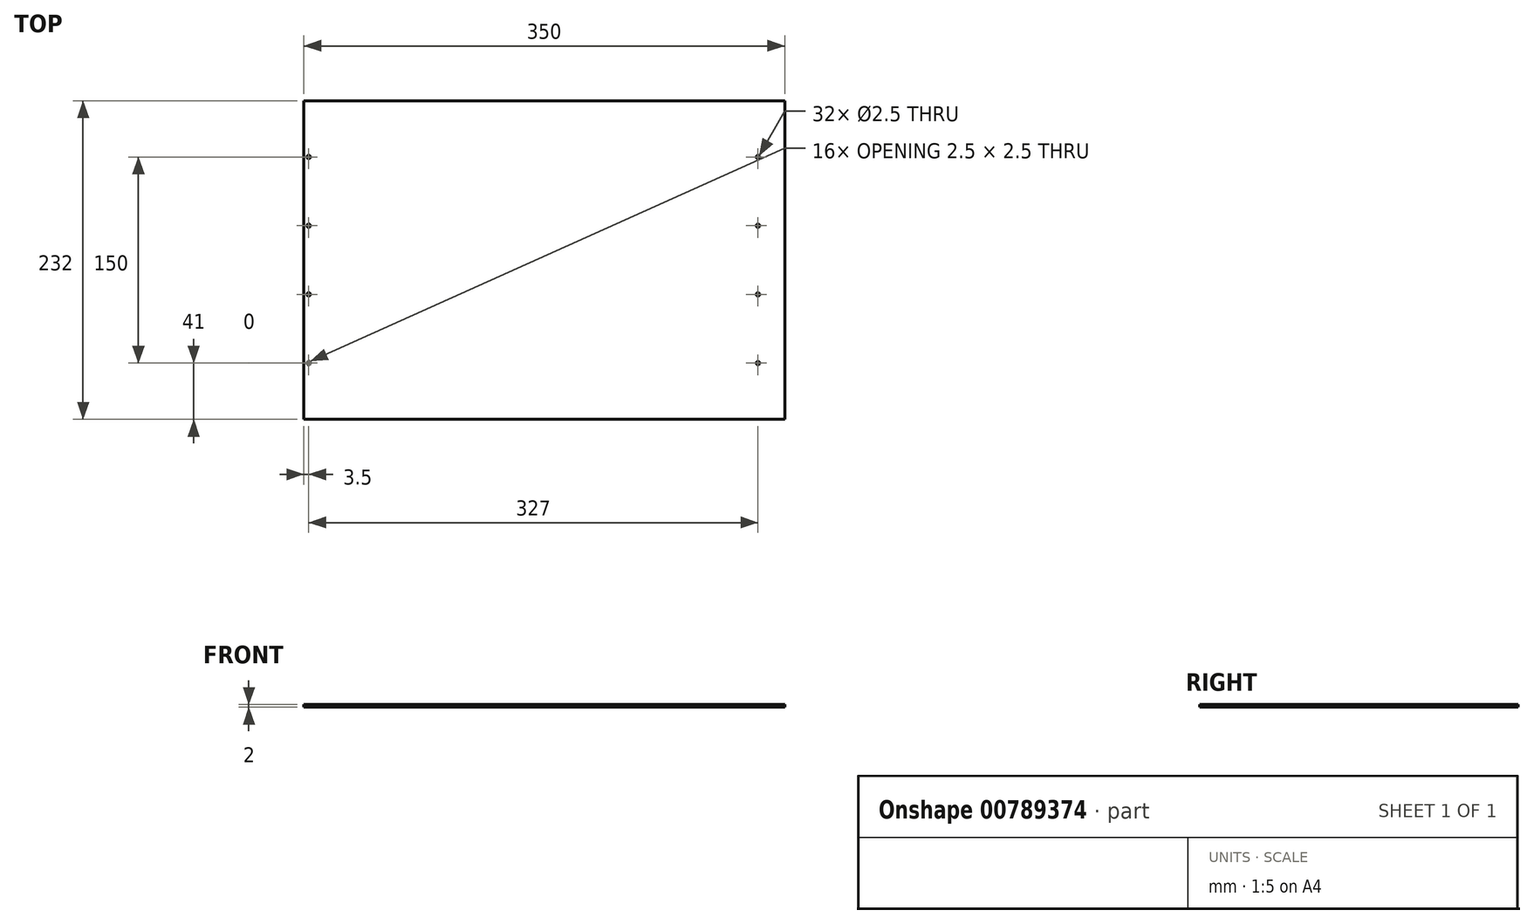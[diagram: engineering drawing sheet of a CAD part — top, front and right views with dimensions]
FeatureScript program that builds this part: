
annotation { "Feature Type Name" : "Feature", "Feature Type Description" : "" }
export const myFeature = defineFeature(function(context is Context, id is Id, definition is map)
    precondition{}
    {
        {
            var Q0;
            Q0=qCreatedBy(makeId("Top.planeOp"),FACE);
            var sketch = newSketch(context, id + "F0", { "sketchPlane" : qUnion([Q0])});
            skLineSegment(sketch, "E0", {"start": v(0, 0) * mm, "end": v(350, 0) * mm});
            skLineSegment(sketch, "E1", {"start": v(350, 0) * mm, "end": v(350, 232) * mm});
            skLineSegment(sketch, "E2", {"start": v(350, 232) * mm, "end": v(0, 232) * mm});
            skLineSegment(sketch, "E3", {"start": v(0, 232) * mm, "end": v(0, 0) * mm});
            skSolve(sketch);
        }
        {
            var Q0;
            Q0 = qSketchRegion(id + "F0", true);
            extrude(context, id + "F1", {"entities" : qUnion([Q0]), "depth" : 2 * mm, "offsetDistance" : 25 * mm});
        }
        {
            var Q0;
            Q0=qCreatedBy(makeId("Top.planeOp"),FACE);
            var sketch = newSketch(context, id + "F2", { "sketchPlane" : qUnion([Q0])});
            skCircle(sketch, "E4", {"center": v(3.5, 41) * mm, "radius": 1.25 * mm});
            skCircle(sketch, "E5", {"center": v(3.5, 91) * mm, "radius": 1.25 * mm});
            skCircle(sketch, "E6", {"center": v(3.5, 191) * mm, "radius": 1.25 * mm});
            skCircle(sketch, "E7", {"center": v(3.5, 141) * mm, "radius": 1.25 * mm});
            skCircle(sketch, "E8", {"center": v(330.5, 191) * mm, "radius": 1.25 * mm});
            skCircle(sketch, "E9", {"center": v(330.5, 141) * mm, "radius": 1.25 * mm});
            skCircle(sketch, "E10", {"center": v(330.5, 91) * mm, "radius": 1.25 * mm});
            skCircle(sketch, "E11", {"center": v(330.5, 41) * mm, "radius": 1.25 * mm});
            skSolve(sketch);
        }
        {
            var Q0;
            Q0=sQuery(id+"F2.wireOp",VERTEX,"E8.center");
            var Q1;
            Q1=sQuery(id+"F2.wireOp",VERTEX,"E9.center");
            var Q2;
            Q2=sQuery(id+"F2.wireOp",VERTEX,"E10.center");
            var Q3;
            Q3=sQuery(id+"F2.wireOp",VERTEX,"E11.center");
            var Q4;
            Q4=sQuery(id+"F2.wireOp",VERTEX,"E6.center");
            var Q5;
            Q5=sQuery(id+"F2.wireOp",VERTEX,"E7.center");
            var Q6;
            Q6=sQuery(id+"F2.wireOp",VERTEX,"E5.center");
            var Q7;
            Q7=sQuery(id+"F2.wireOp",VERTEX,"E4.center");
            var Q8;
            Q8=makeQuery(id+"F1.opExtrude","SWEPT_BODY",BODY,{"disambiguationData":[OSD([sQuery(id+"F0.wireOp",EDGE,"E0"),sQuery(id+"F0.wireOp",EDGE,"E1"),sQuery(id+"F0.wireOp",EDGE,"E2"),sQuery(id+"F0.wireOp",EDGE,"E3")])]});
            hole(context, id + "F3", {"style" : HoleStyle.SIMPLE, "endStyle" : HoleEndStyle.THROUGH, "oppositeDirection" : true, "holeDiameter" : 2.5 * mm, "majorDiameter" : 5 * mm, "isTappedThrough" : true, "tappedDepth" : 12 * mm, "tapClearance" : 3, "locations" : qUnion([Q0, Q1, Q2, Q3, Q4, Q5, Q6, Q7]), "scope" : qUnion([Q8])});
        }
    });
